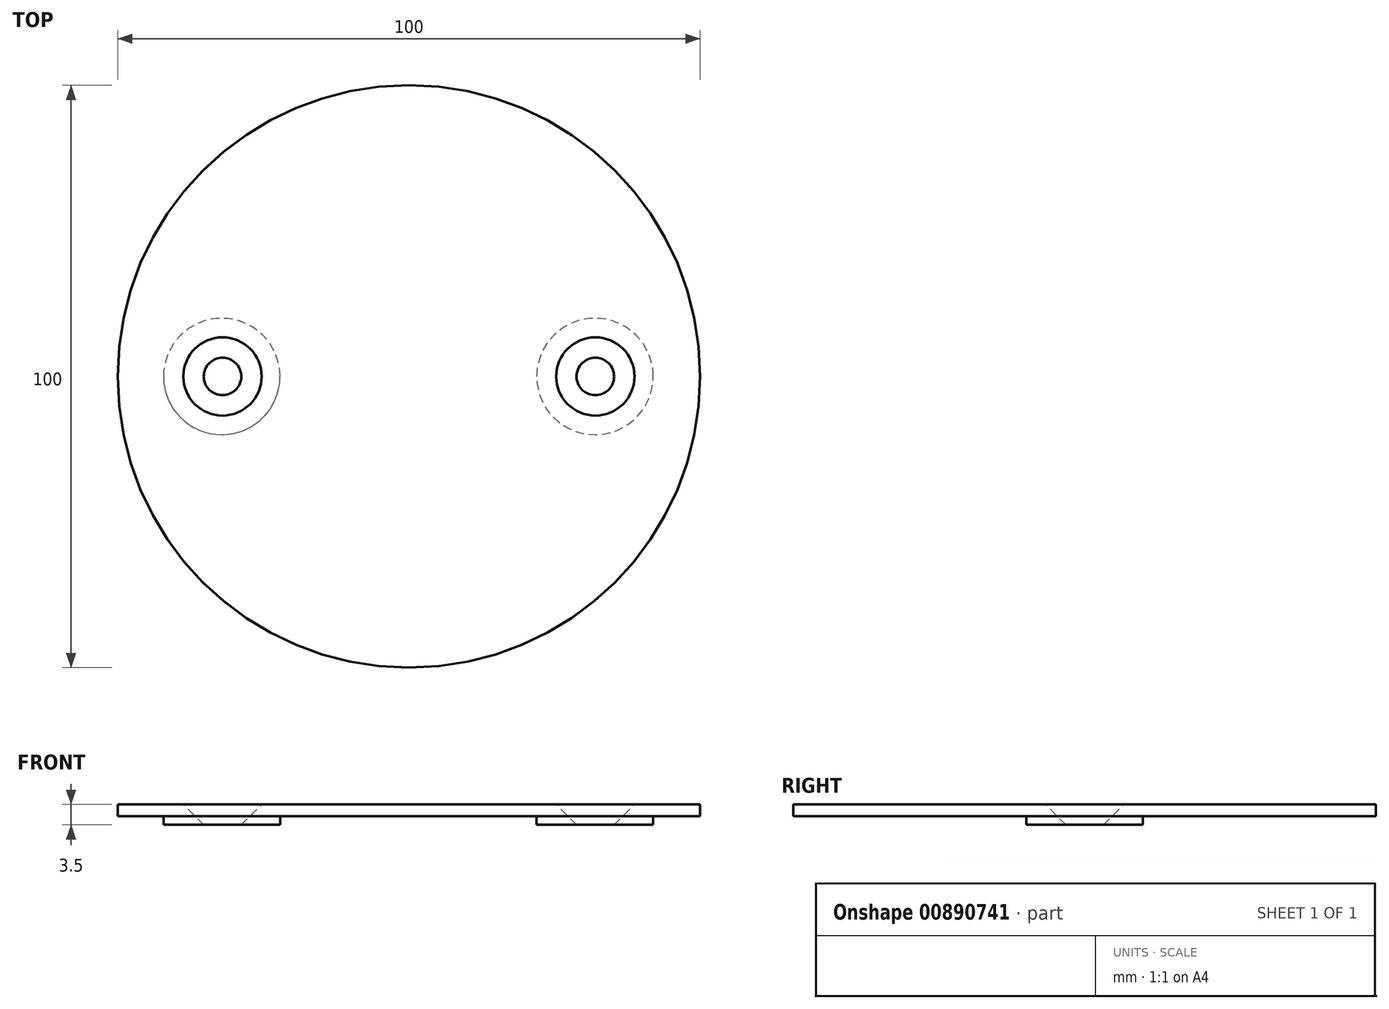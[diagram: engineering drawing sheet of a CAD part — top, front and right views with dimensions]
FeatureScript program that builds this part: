
annotation { "Feature Type Name" : "Feature", "Feature Type Description" : "" }
export const myFeature = defineFeature(function(context is Context, id is Id, definition is map)
    precondition{}
    {
        {
            var Q0;
            Q0=qCreatedBy(makeId("Top.planeOp"),FACE);
            var sketch = newSketch(context, id + "F0", { "sketchPlane" : qUnion([Q0])});
            skCircle(sketch, "E0", {"center": v(0, 0) * mm, "radius": 50 * mm});
            skSolve(sketch);
        }
        {
            var Q0;
            Q0 = qSketchRegion(id + "F0", true);
            extrude(context, id + "F1", {"entities" : qUnion([Q0]), "depth" : 2 * mm, "offsetDistance" : 25 * mm});
        }
        {
            var Q0;
            Q0=makeQuery(id+"F1.opExtrude","CAP_FACE",FACE,{"disambiguationData":[OSD([sQuery(id+"F0.wireOp",EDGE,"E0")])],"isStart":false});
            var sketch = newSketch(context, id + "F2", { "sketchPlane" : qUnion([Q0])});
            skLineSegment(sketch, "E1", {"start": v(-50, 0) * mm, "end": v(50, 0) * mm, "construction": true});
            skPoint(sketch, "E2", {"position": v(-32, 0) * mm});
            skPoint(sketch, "E3", {"position": v(32, 0) * mm});
            skSolve(sketch);
        }
        {
            var Q0;
            Q0=makeQuery(id+"F1.opExtrude","CAP_FACE",FACE,{"disambiguationData":[OSD([sQuery(id+"F0.wireOp",EDGE,"E0")])],"isStart":true});
            var sketch = newSketch(context, id + "F3", { "sketchPlane" : qUnion([Q0])});
            skCircle(sketch, "E4", {"center": v(31.94, 0) * mm, "radius": 10 * mm});
            skCircle(sketch, "E5", {"center": v(-32.13, 0) * mm, "radius": 10 * mm});
            skSolve(sketch);
        }
        {
            var Q0;
            Q0 = qSketchRegion(id + "F3", true);
            extrude(context, id + "F4", {"entities" : qUnion([Q0]), "operationType" : NewBodyOperationType.ADD, "depth" : 1.5 * mm, "offsetDistance" : 25 * mm});
        }
        {
            var Q0;
            Q0=sQuery(id+"F2.wireOp",VERTEX,"E2");
            var Q1;
            Q1=sQuery(id+"F2.wireOp",VERTEX,"E3");
            var Q2;
            Q2=makeQuery(id+"F1.opExtrude","SWEPT_BODY",BODY,{"disambiguationData":[OSD([sQuery(id+"F0.wireOp",EDGE,"E0")])]});
            hole(context, id + "F5", {"style" : HoleStyle.C_SINK, "endStyle" : HoleEndStyle.THROUGH, "standardTappedOrClearance" : lookupTablePath({ "fit" : "Close", "standard" : "ISO", "size" : "M6", "type" : "Clearance" }), "standardBlindInLast" : lookupTablePath({ "fit" : "Close", "standard" : "ISO", "size" : "M6", "type" : "Clearance" }), "holeDiameter" : 6.4 * mm, "cSinkDiameter" : 13.44 * mm, "cSinkAngle" : 90 * degree, "majorDiameter" : 5 * mm, "isTappedThrough" : true, "tappedDepth" : 12 * mm, "tapClearance" : 3, "locations" : qUnion([Q0, Q1]), "scope" : qUnion([Q2])});
        }
    });
